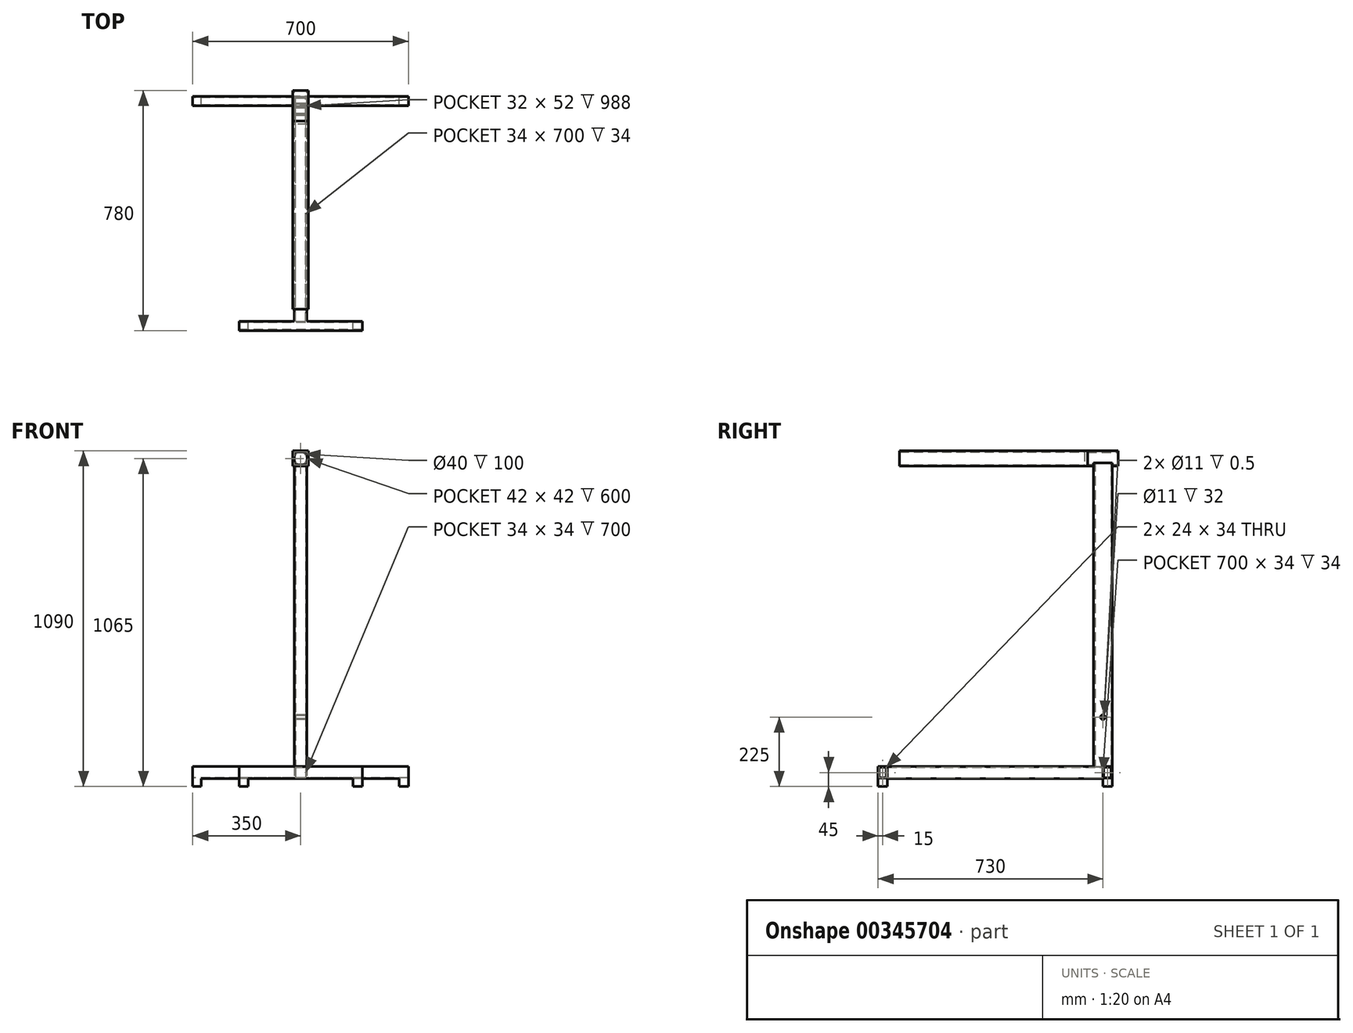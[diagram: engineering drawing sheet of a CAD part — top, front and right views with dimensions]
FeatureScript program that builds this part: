
annotation { "Feature Type Name" : "Feature", "Feature Type Description" : "" }
export const myFeature = defineFeature(function(context is Context, id is Id, definition is map)
    precondition{}
    {
        {
            var Q0;
            Q0=qCreatedBy(makeId("Front.planeOp"),FACE);
            var sketch = newSketch(context, id + "F0", { "sketchPlane" : qUnion([Q0])});
            skCircle(sketch, "E0", {"center": v(0, 0) * mm, "radius": 25 * mm});
            skCircle(sketch, "E1", {"center": v(0, 0) * mm, "radius": 20 * mm});
            skLineSegment(sketch, "E2.top", {"start": v(20, -1000) * mm, "end": v(-20, -1000) * mm});
            skLineSegment(sketch, "E2.left", {"start": v(20, -15) * mm, "end": v(20, -1000) * mm});
            skLineSegment(sketch, "E2.right", {"start": v(-20, -15) * mm, "end": v(-20, -1000) * mm});
            skPoint(sketch, "E2.middle", {"position": v(0, -507.5) * mm});
            skSolve(sketch);
        }
        {
            var Q0;
            Q0=makeQuery(id+"F0.imprint","IMPRINT",FACE,{"disambiguationData":[TD([[makeQuery(id+"F0.imprint","IMPRINT",EDGE,{"derivedFrom":sQuery(id+"F0.wireOp",EDGE,"E0")}),1.0]])]});
            extrude(context, id + "F1", {"entities" : qUnion([Q0]), "endBound" : BoundingType.SYMMETRIC, "depth" : 100 * mm});
        }
        {
            var Q0;
            Q0=makeQuery(id+"F0.imprint","IMPRINT",FACE,{"disambiguationData":[TD([[makeQuery(id+"F0.imprint","IMPRINT",EDGE,{"derivedFrom":sQuery(id+"F0.wireOp",EDGE,"E2.top")}),-1.0]])]});
            extrude(context, id + "F2", {"entities" : qUnion([Q0]), "operationType" : NewBodyOperationType.ADD, "endBound" : BoundingType.SYMMETRIC, "depth" : 60 * mm});
        }
        {
            var Q0;
            Q0=makeQuery(id+"F2.opExtrude","SWEPT_FACE",FACE,{"disambiguationData":[OSD([sQuery(id+"F0.wireOp",EDGE,"E2.top")])]});
            var sketch = newSketch(context, id + "F3", { "sketchPlane" : qUnion([Q0])});
            skLineSegment(sketch, "E3.bottom", {"start": v(16, 26) * mm, "end": v(-16, 26) * mm});
            skLineSegment(sketch, "E3.top", {"start": v(16, -26) * mm, "end": v(-16, -26) * mm});
            skLineSegment(sketch, "E3.left", {"start": v(16, 26) * mm, "end": v(16, -26) * mm});
            skLineSegment(sketch, "E3.right", {"start": v(-16, 26) * mm, "end": v(-16, -26) * mm});
            skPoint(sketch, "E3.middle", {"position": v(0, 0) * mm});
            skSolve(sketch);
        }
        {
            var Q0;
            Q0=makeQuery(id+"F3.imprint","IMPRINT",FACE,{"disambiguationData":[TD([[makeQuery(id+"F3.imprint","IMPRINT",EDGE,{"derivedFrom":sQuery(id+"F3.wireOp",EDGE,"E3.bottom")}),1.0]])]});
            extrude(context, id + "F4", {"entities" : qUnion([Q0]), "operationType" : NewBodyOperationType.REMOVE, "endBound" : BoundingType.UP_TO_NEXT, "oppositeDirection" : true, "depth" : 976.9 * mm});
        }
        {
            var Q0;
            Q0=qCreatedBy(makeId("Right.planeOp"),FACE);
            var sketch = newSketch(context, id + "F5", { "sketchPlane" : qUnion([Q0])});
            skLineSegment(sketch, "E4.bottom", {"start": v(0, -1000) * mm, "end": v(30, -1000) * mm});
            skLineSegment(sketch, "E4.top", {"start": v(0, -1040) * mm, "end": v(30, -1040) * mm});
            skLineSegment(sketch, "E4.left", {"start": v(0, -1000) * mm, "end": v(0, -1040) * mm});
            skLineSegment(sketch, "E4.right", {"start": v(30, -1000) * mm, "end": v(30, -1040) * mm});
            skLineSegment(sketch, "E5.bottom", {"start": v(27, -1037) * mm, "end": v(3, -1037) * mm});
            skLineSegment(sketch, "E5.top", {"start": v(27, -1003) * mm, "end": v(3, -1003) * mm});
            skLineSegment(sketch, "E5.left", {"start": v(27, -1037) * mm, "end": v(27, -1003) * mm});
            skLineSegment(sketch, "E5.right", {"start": v(3, -1037) * mm, "end": v(3, -1003) * mm});
            skPoint(sketch, "E5.middle", {"position": v(15, -1020) * mm});
            skPoint(sketch, "E5.middle.positionSnap0", {"position": v(30, -1020) * mm});
            skPoint(sketch, "E5.middle.positionSnap1", {"position": v(15, -1040) * mm});
            skPoint(sketch, "E5.centerSnap0", {"position": v(30, -1020) * mm});
            skPoint(sketch, "E5.centerSnap1", {"position": v(15, -1040) * mm});
            skLineSegment(sketch, "E6.bottom", {"start": v(-700, -1000) * mm, "end": v(-730, -1000) * mm});
            skLineSegment(sketch, "E6.top", {"start": v(-700, -1040) * mm, "end": v(-730, -1040) * mm});
            skLineSegment(sketch, "E6.left", {"start": v(-700, -1000) * mm, "end": v(-700, -1040) * mm});
            skLineSegment(sketch, "E6.right", {"start": v(-730, -1000) * mm, "end": v(-730, -1040) * mm});
            skPoint(sketch, "E6.middle", {"position": v(-715, -1020) * mm});
            skLineSegment(sketch, "E7.bottom", {"start": v(-703, -1003) * mm, "end": v(-727, -1003) * mm});
            skLineSegment(sketch, "E7.top", {"start": v(-703, -1037) * mm, "end": v(-727, -1037) * mm});
            skLineSegment(sketch, "E7.left", {"start": v(-703, -1003) * mm, "end": v(-703, -1037) * mm});
            skLineSegment(sketch, "E7.right", {"start": v(-727, -1003) * mm, "end": v(-727, -1037) * mm});
            skLineSegment(sketch, "E8", {"start": v(0, -1040) * mm, "end": v(-700, -1040) * mm});
            skLineSegment(sketch, "E9", {"start": v(-700, -1000) * mm, "end": v(0, -1000) * mm});
            skSolve(sketch);
        }
        {
            var Q0;
            Q0=makeQuery(id+"F5.imprint","IMPRINT",FACE,{"disambiguationData":[TD([[makeQuery(id+"F5.imprint","IMPRINT",EDGE,{"derivedFrom":sQuery(id+"F5.wireOp",EDGE,"E4.bottom")}),-1.0]])]});
            extrude(context, id + "F6", {"entities" : qUnion([Q0]), "operationType" : NewBodyOperationType.ADD, "endBound" : BoundingType.SYMMETRIC, "depth" : 700 * mm});
        }
        {
            var Q0;
            Q0=makeQuery(id+"F6.opExtrude","SWEPT_FACE",FACE,{"disambiguationData":[OSD([sQuery(id+"F5.wireOp",EDGE,"E4.left")])]});
            var sketch = newSketch(context, id + "F7", { "sketchPlane" : qUnion([Q0])});
            skLineSegment(sketch, "E10", {"start": v(-20, -1000) * mm, "end": v(-20, -1020) * mm});
            skLineSegment(sketch, "E11", {"start": v(-20, -1020) * mm, "end": v(0, -1020) * mm});
            skLineSegment(sketch, "E12.bottom", {"start": v(-20, -1000) * mm, "end": v(20, -1000) * mm});
            skLineSegment(sketch, "E12.top", {"start": v(-20, -1040) * mm, "end": v(20, -1040) * mm});
            skLineSegment(sketch, "E12.left", {"start": v(-20, -1000) * mm, "end": v(-20, -1040) * mm});
            skLineSegment(sketch, "E12.right", {"start": v(20, -1000) * mm, "end": v(20, -1040) * mm});
            skPoint(sketch, "E12.middle", {"position": v(0, -1020) * mm});
            skLineSegment(sketch, "E13.bottom", {"start": v(-17, -1003) * mm, "end": v(17, -1003) * mm});
            skLineSegment(sketch, "E13.top", {"start": v(-17, -1037) * mm, "end": v(17, -1037) * mm});
            skLineSegment(sketch, "E13.left", {"start": v(-17, -1003) * mm, "end": v(-17, -1037) * mm});
            skLineSegment(sketch, "E13.right", {"start": v(17, -1003) * mm, "end": v(17, -1037) * mm});
            skSolve(sketch);
        }
        {
            var Q0;
            {var subQ7=sQuery(id+"F7.wireOp",EDGE,"E12.top");Q0=makeQuery(id+"F7.imprint","IMPRINT",FACE,{"disambiguationData":[TD([[makeQuery(id+"F7.imprint","IMPRINT",EDGE,{"derivedFrom":subQ7}),-1.0]])]});}
            extrude(context, id + "F8", {"entities" : qUnion([Q0]), "operationType" : NewBodyOperationType.ADD, "depth" : 700 * mm});
        }
        {
            var Q0;
            Q0=makeQuery(id+"F5.imprint","IMPRINT",FACE,{"disambiguationData":[TD([[makeQuery(id+"F5.imprint","IMPRINT",EDGE,{"derivedFrom":sQuery(id+"F5.wireOp",EDGE,"E6.bottom")}),1.0]])]});
            extrude(context, id + "F9", {"entities" : qUnion([Q0]), "operationType" : NewBodyOperationType.ADD, "endBound" : BoundingType.SYMMETRIC, "depth" : 400 * mm});
        }
        {
            var Q0;
            Q0=makeQuery(id+"F9.boolean.opBoolean","MERGE",FACE,{"derivedFrom":[makeQuery(id+"F8.boolean.opBoolean","MERGE",FACE,{"derivedFrom":[makeQuery(id+"F6.opExtrude","SWEPT_FACE",FACE,{"disambiguationData":[OSD([sQuery(id+"F5.wireOp",EDGE,"E4.top")])]}),makeQuery(id+"F8.opExtrude","SWEPT_FACE",FACE,{"disambiguationData":[OSD([sQuery(id+"F7.wireOp",EDGE,"E12.top")])]})]}),makeQuery(id+"F9.opExtrude","SWEPT_FACE",FACE,{"disambiguationData":[OSD([sQuery(id+"F5.wireOp",EDGE,"E6.top")])]})]});
            var sketch = newSketch(context, id + "F10", { "sketchPlane" : qUnion([Q0])});
            skLineSegment(sketch, "E14.bottom", {"start": v(-350, 0) * mm, "end": v(-322.1, 0) * mm});
            skLineSegment(sketch, "E14.top", {"start": v(-350, -30) * mm, "end": v(-322.1, -30) * mm});
            skLineSegment(sketch, "E14.left", {"start": v(-350, 0) * mm, "end": v(-350, -30) * mm});
            skLineSegment(sketch, "E14.right", {"start": v(-322.1, 0) * mm, "end": v(-322.1, -30) * mm});
            skLineSegment(sketch, "E15.bottom", {"start": v(350, 0) * mm, "end": v(320.32, 0) * mm});
            skLineSegment(sketch, "E15.top", {"start": v(350, -30) * mm, "end": v(320.32, -30) * mm});
            skLineSegment(sketch, "E15.left", {"start": v(350, 0) * mm, "end": v(350, -30) * mm});
            skLineSegment(sketch, "E15.right", {"start": v(320.32, 0) * mm, "end": v(320.32, -30) * mm});
            skLineSegment(sketch, "E16.bottom", {"start": v(-200, 730) * mm, "end": v(-170.27, 730) * mm});
            skLineSegment(sketch, "E16.top", {"start": v(-200, 700) * mm, "end": v(-170.27, 700) * mm});
            skLineSegment(sketch, "E16.left", {"start": v(-200, 730) * mm, "end": v(-200, 700) * mm});
            skLineSegment(sketch, "E16.right", {"start": v(-170.27, 730) * mm, "end": v(-170.27, 700) * mm});
            skLineSegment(sketch, "E17.bottom", {"start": v(200, 730) * mm, "end": v(170.29, 730) * mm});
            skLineSegment(sketch, "E17.top", {"start": v(200, 700) * mm, "end": v(170.29, 700) * mm});
            skLineSegment(sketch, "E17.left", {"start": v(200, 730) * mm, "end": v(200, 700) * mm});
            skLineSegment(sketch, "E17.right", {"start": v(170.29, 730) * mm, "end": v(170.29, 700) * mm});
            skSolve(sketch);
        }
        {
            var Q0;
            Q0=qSketchRegion(id+"F10",true);
            extrude(context, id + "F11", {"entities" : qUnion([Q0]), "operationType" : NewBodyOperationType.ADD, "depth" : 25 * mm});
        }
        {
            var Q0;
            Q0=makeQuery(id+"F1.opExtrude","CAP_FACE",FACE,{"disambiguationData":[OSD([sQuery(id+"F0.wireOp",EDGE,"E0"),sQuery(id+"F0.wireOp",EDGE,"E1")])],"isStart":false});
            var sketch = newSketch(context, id + "F12", { "sketchPlane" : qUnion([Q0])});
            skLineSegment(sketch, "E18.bottom", {"start": v(-25, 25) * mm, "end": v(25, 25) * mm});
            skLineSegment(sketch, "E18.top", {"start": v(-25, -25) * mm, "end": v(25, -25) * mm});
            skLineSegment(sketch, "E18.left", {"start": v(-25, 25) * mm, "end": v(-25, -25) * mm});
            skLineSegment(sketch, "E18.right", {"start": v(25, 25) * mm, "end": v(25, -25) * mm});
            skPoint(sketch, "E18.middle", {"position": v(0, 0) * mm});
            skSolve(sketch);
        }
        {
            var Q0;
            Q0 = qSketchRegion(id + "F12", true);
            extrude(context, id + "F13", {"entities" : qUnion([Q0]), "operationType" : NewBodyOperationType.ADD, "depth" : 10 * mm});
        }
        {
            var Q0;
            Q0=makeQuery(id+"F13.opExtrude","CAP_FACE",FACE,{"disambiguationData":[OSD([sQuery(id+"F12.wireOp",EDGE,"E18.bottom"),sQuery(id+"F12.wireOp",EDGE,"E18.top"),sQuery(id+"F12.wireOp",EDGE,"E18.left"),sQuery(id+"F12.wireOp",EDGE,"E18.right")])],"isStart":false});
            var sketch = newSketch(context, id + "F14", { "sketchPlane" : qUnion([Q0])});
            skLineSegment(sketch, "E19.bottom", {"start": v(21, 21) * mm, "end": v(-21, 21) * mm});
            skLineSegment(sketch, "E19.top", {"start": v(21, -21) * mm, "end": v(-21, -21) * mm});
            skLineSegment(sketch, "E19.left", {"start": v(21, 21) * mm, "end": v(21, -21) * mm});
            skLineSegment(sketch, "E19.right", {"start": v(-21, 21) * mm, "end": v(-21, -21) * mm});
            skPoint(sketch, "E19.middle", {"position": v(0, 0) * mm});
            skLineSegment(sketch, "E20.bottom", {"start": v(-25, 25) * mm, "end": v(25, 25) * mm});
            skLineSegment(sketch, "E20.top", {"start": v(-25, -25) * mm, "end": v(25, -25) * mm});
            skLineSegment(sketch, "E20.left", {"start": v(-25, 25) * mm, "end": v(-25, -25) * mm});
            skLineSegment(sketch, "E20.right", {"start": v(25, 25) * mm, "end": v(25, -25) * mm});
            skSolve(sketch);
        }
        {
            var Q0;
            Q0 = qSketchRegion(id + "F14", true);
            extrude(context, id + "F15", {"entities" : qUnion([Q0]), "operationType" : NewBodyOperationType.ADD, "depth" : 600 * mm});
        }
        {
            var Q0;
            Q0=qCreatedBy(makeId("Right.planeOp"),FACE);
            var sketch = newSketch(context, id + "F16", { "sketchPlane" : qUnion([Q0])});
            skCircle(sketch, "E21", {"center": v(0, -840) * mm, "radius": 5.5 * mm});
            skCircle(sketch, "E22", {"center": v(0, -840) * mm, "radius": 7.5 * mm});
            skSolve(sketch);
        }
        {
            var Q0;
            Q0 = qSketchRegion(id + "F16", true);
            extrude(context, id + "F17", {"entities" : qUnion([Q0]), "operationType" : NewBodyOperationType.ADD, "endBound" : BoundingType.SYMMETRIC, "depth" : 41 * mm});
        }
        {
            var Q0;
            Q0=sQuery(id+"F16.wireOp",EDGE,"E21");
            extrude(context, id + "F18", {"bodyType" : ToolBodyType.SURFACE, "surfaceEntities" : qUnion([Q0]), "endBound" : BoundingType.SYMMETRIC, "depth" : 40 * mm});
        }
    });
